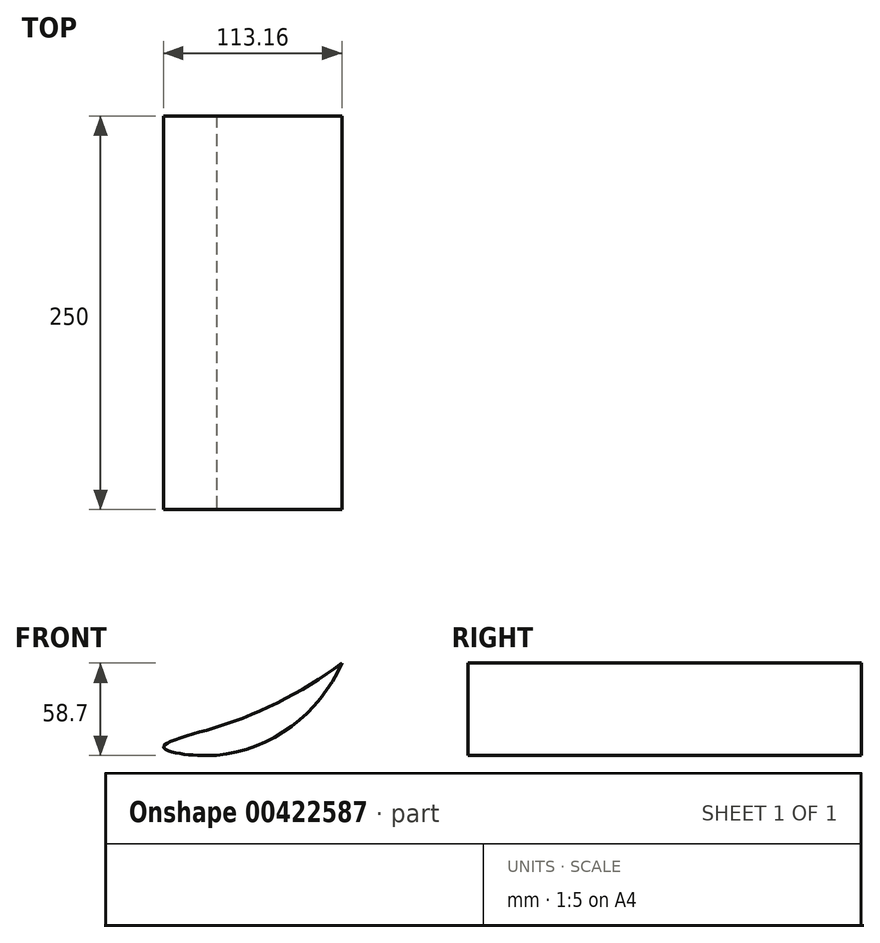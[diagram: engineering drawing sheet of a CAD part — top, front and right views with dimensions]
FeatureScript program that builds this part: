
annotation { "Feature Type Name" : "Feature", "Feature Type Description" : "" }
export const myFeature = defineFeature(function(context is Context, id is Id, definition is map)
    precondition{}
    {
        {
            var Q0;
            Q0=qCreatedBy(makeId("Front.planeOp"),FACE);
            cPlane(context, id + "F0", {"entities" : qUnion([Q0]), "cplaneType" : CPlaneType.OFFSET, "offset" : 253 * mm, "oppositeDirection" : true, "width" : 150 * mm, "height" : 150 * mm});
        }
        {
            var Q0;
            Q0=qCreatedBy(id+"F0.planeOp",FACE);
            var sketch = newSketch(context, id + "F1", { "sketchPlane" : qUnion([Q0])});
            skPoint(sketch, "E0", {"position": v(-917.28, 223.49) * mm});
            skPoint(sketch, "E1", {"position": v(-996.95, 164.79) * mm});
            skPoint(sketch, "E2", {"position": v(-1021, 166.15) * mm});
            skPoint(sketch, "E3", {"position": v(-1030.44, 170.24) * mm});
            skPoint(sketch, "E4", {"position": v(-1003.16, 180.87) * mm});
            skArc(sketch, "E5", {"start": v(-1003.16, 180.87) * mm, "mid": v(-958.24, 198.2) * mm, "end": v(-917.28, 223.49) * mm});
            skFitSpline(sketch, "E6", {"points": [v(-996.95, 164.79) * mm, v(-1021, 166.15) * mm, v(-1030.44, 170.24) * mm, v(-1003.16, 180.87) * mm], "startDerivative": vector(-68.27, 0.05) * mm, "endDerivative": vector(101.69, 28.74) * mm});
            skArc(sketch, "E7", {"start": v(-996.95, 164.79) * mm, "mid": v(-949.17, 183.35) * mm, "end": v(-917.28, 223.49) * mm});
            skSolve(sketch);
        }
        {
            var Q0;
            Q0=makeQuery(id+"F1.imprint","IMPRINT",FACE,{"disambiguationData":[TD([[makeQuery(id+"F1.imprint","IMPRINT",EDGE,{"derivedFrom":sQuery(id+"F1.wireOp",EDGE,"E5")}),-1.0]])]});
            extrude(context, id + "F2", {"entities" : qUnion([Q0]), "oppositeDirection" : true, "depth" : 250 * mm});
        }
    });
